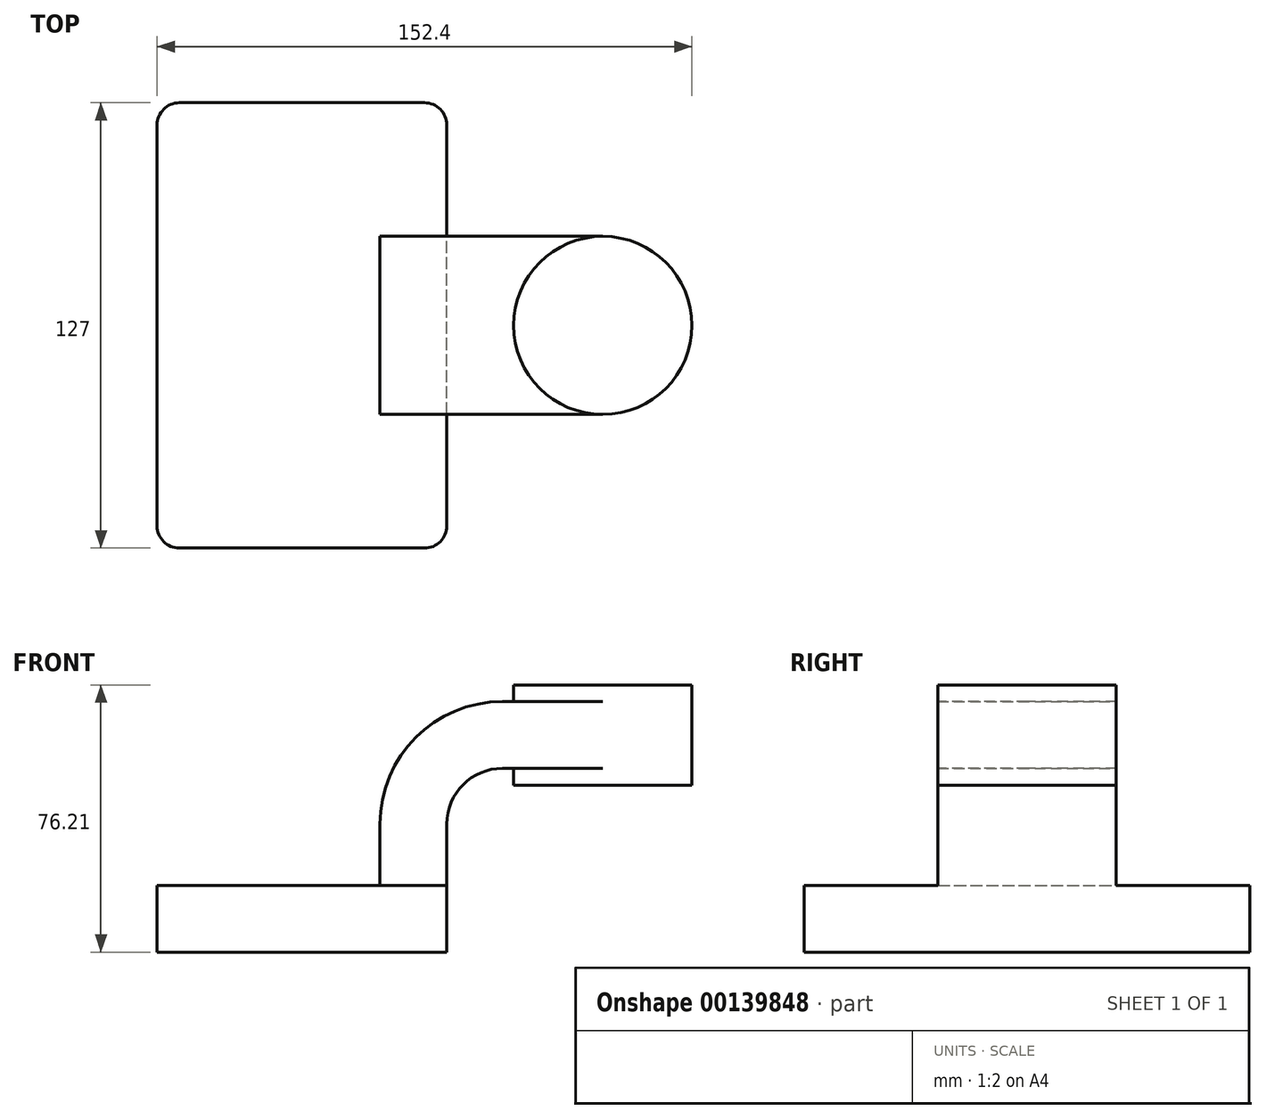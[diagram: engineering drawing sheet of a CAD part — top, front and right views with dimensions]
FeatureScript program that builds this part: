
annotation { "Feature Type Name" : "Feature", "Feature Type Description" : "" }
export const myFeature = defineFeature(function(context is Context, id is Id, definition is map)
    precondition{}
    {
        {
            var Q0;
            Q0=qCreatedBy(makeId("Front.planeOp"),FACE);
            var sketch = newSketch(context, id + "F0", { "sketchPlane" : qUnion([Q0])});
            skLineSegment(sketch, "E0.bottom", {"start": v(-41.28, 9.52) * mm, "end": v(41.27, 9.53) * mm});
            skLineSegment(sketch, "E0.top", {"start": v(-41.28, -9.53) * mm, "end": v(41.28, -9.53) * mm});
            skLineSegment(sketch, "E0.left", {"start": v(-41.28, 9.52) * mm, "end": v(-41.27, -9.53) * mm});
            skLineSegment(sketch, "E0.right", {"start": v(41.28, 9.53) * mm, "end": v(41.28, -9.52) * mm});
            skPoint(sketch, "E0.middle", {"position": v(0, 0) * mm});
            skLineSegment(sketch, "E1.bottom", {"start": v(60.32, 66.68) * mm, "end": v(111.12, 66.68) * mm});
            skLineSegment(sketch, "E1.top", {"start": v(60.32, 38.1) * mm, "end": v(111.12, 38.1) * mm});
            skLineSegment(sketch, "E1.left", {"start": v(60.32, 66.68) * mm, "end": v(60.32, 38.1) * mm});
            skLineSegment(sketch, "E1.right", {"start": v(111.12, 66.68) * mm, "end": v(111.12, 38.1) * mm});
            skPoint(sketch, "E1.middle", {"position": v(85.72, 52.39) * mm});
            skLineSegment(sketch, "E2", {"start": v(41.27, 9.53) * mm, "end": v(41.27, 27) * mm});
            skArc(sketch, "E3", {"start": v(41.27, 27) * mm, "mid": v(45.92, 38.23) * mm, "end": v(57.15, 42.88) * mm});
            skLineSegment(sketch, "E4.0", {"start": v(57.15, 61.93) * mm, "end": v(85.72, 61.93) * mm});
            skArc(sketch, "E4.1", {"start": v(22.23, 27) * mm, "mid": v(32.45, 51.7) * mm, "end": v(57.15, 61.93) * mm});
            skLineSegment(sketch, "E4.2", {"start": v(22.22, 9.53) * mm, "end": v(22.22, 27) * mm});
            skFitSpline(sketch, "E5", {"points": [v(-41.28, 9.53) * mm, v(57.15, 61.93) * mm], "startDerivative": vector(0.63, 70.67) * mm, "endDerivative": vector(132.45, 0) * mm});
            skLineSegment(sketch, "E6", {"start": v(85.72, 38.1) * mm, "end": v(85.72, 66.67) * mm});
            skLineSegment(sketch, "E7", {"start": v(57.15, 42.88) * mm, "end": v(85.72, 42.88) * mm});
            skSolve(sketch);
        }
        {
            var Q0;
            Q0=makeQuery(id+"F0.imprint","IMPRINT",FACE,{"disambiguationData":[TD([[makeQuery(id+"F0.imprint","IMPRINT",EDGE,{"derivedFrom":sQuery(id+"F0.wireOp",EDGE,"E0.top")}),1.0]])]});
            extrude(context, id + "F1", {"entities" : qUnion([Q0]), "endBound" : BoundingType.SYMMETRIC, "depth" : 127 * mm});
        }
        {
            var Q0;
            Q0=makeQuery(id+"F0.imprint","IMPRINT",FACE,{"disambiguationData":[TD([[makeQuery(id+"F0.imprint","IMPRINT",EDGE,{"derivedFrom":sQuery(id+"F0.wireOp",EDGE,"E0.top")}),1.0]])]});
            var Q1;
            {var subQ2=sQuery(id+"F0.wireOp",EDGE,"E2");Q1=makeQuery(id+"F0.imprint","IMPRINT",FACE,{"disambiguationData":[TD([[makeQuery(id+"F0.imprint","IMPRINT",EDGE,{"derivedFrom":subQ2}),1.0]])]});}
            var Q2;
            {var subQ0=sQuery(id+"F0.wireOp",EDGE,"E4.0");var subQ1=sQuery(id+"F0.wireOp",EDGE,"E1.left");var subQ2=makeQuery(id+"F0.imprint","INTERSECT",VERTEX,{"derivedFrom":[subQ1,subQ0]});Q2=makeQuery(id+"F0.imprint","IMPRINT",FACE,{"disambiguationData":[TD([[makeQuery(id+"F0.imprint","IMPRINT",EDGE,{"disambiguationData":[TD([[subQ2,-1.0]])],"derivedFrom":subQ1}),1.0]])]});}
            extrude(context, id + "F2", {"entities" : qUnion([Q0, Q1, Q2]), "operationType" : NewBodyOperationType.ADD, "endBound" : BoundingType.SYMMETRIC, "depth" : 50.8 * mm});
        }
        {
            var Q0;
            Q0=makeQuery(id+"F0.imprint","IMPRINT",FACE,{"disambiguationData":[TD([[makeQuery(id+"F0.imprint","IMPRINT",EDGE,{"derivedFrom":sQuery(id+"F0.wireOp",EDGE,"E4.1")}),1.0]])]});
            extrude(context, id + "F3", {"entities" : qUnion([Q0]), "operationType" : NewBodyOperationType.ADD, "endBound" : BoundingType.SYMMETRIC, "depth" : 15.88 * mm});
        }
        {
            var Q0;
            {var subQ0=sQuery(id+"F0.wireOp",EDGE,"E1.right");Q0=makeQuery(id+"F0.imprint","IMPRINT",FACE,{"disambiguationData":[TD([[makeQuery(id+"F0.imprint","IMPRINT",EDGE,{"derivedFrom":subQ0}),-1.0]])]});}
            var Q1;
            Q1=sQuery(id+"F0.wireOp",EDGE,"E6");
            revolve(context, id + "F4", {"operationType" : NewBodyOperationType.ADD, "entities" : qUnion([Q0]), "axis" : qUnion([Q1]), "revolveType" : RevolveType.FULL});
        }
        {
            var Q0;
            Q0=makeQuery(id+"F1.opExtrude","CAP_EDGE",EDGE,{"disambiguationData":[OSD([sQuery(id+"F0.wireOp",EDGE,"E0.left")])],"isStart":false});
            var Q1;
            Q1=makeQuery(id+"F1.opExtrude","CAP_EDGE",EDGE,{"disambiguationData":[OSD([sQuery(id+"F0.wireOp",EDGE,"E0.right")])],"isStart":false});
            var Q2;
            Q2=makeQuery(id+"F1.opExtrude","CAP_EDGE",EDGE,{"disambiguationData":[OSD([sQuery(id+"F0.wireOp",EDGE,"E0.right")])],"isStart":true});
            var Q3;
            Q3=makeQuery(id+"F1.opExtrude","CAP_EDGE",EDGE,{"disambiguationData":[OSD([sQuery(id+"F0.wireOp",EDGE,"E0.left")])],"isStart":true});
            fillet(context, id + "F5", {"entities" : qUnion([Q0, Q1, Q2, Q3]), "radius" : 6.35 * mm, "tangentPropagation" : true, "allowEdgeOverflow" : false});
        }
    });
